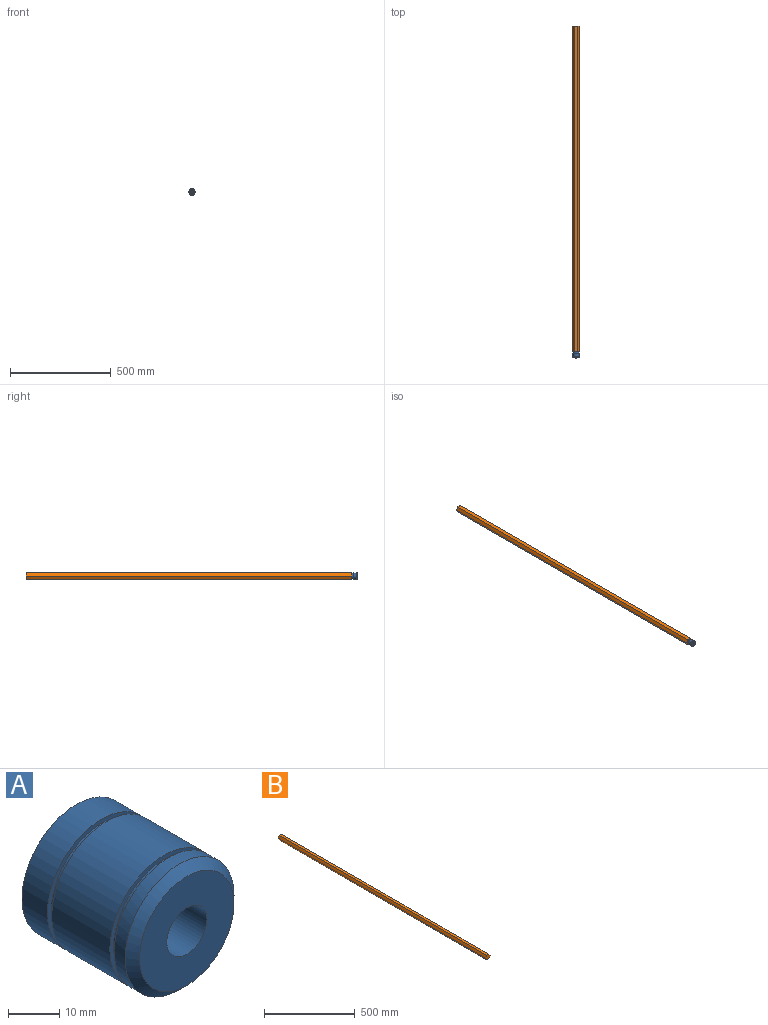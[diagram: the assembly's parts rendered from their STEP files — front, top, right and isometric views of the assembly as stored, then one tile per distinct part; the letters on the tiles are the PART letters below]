
ASSEMBLY  parts=2 mates=1
PART A: 14 faces, bbox 30x30.4x30 mm
  f0: plane 26x26mm, normal (0,-1,0), area 435.9mm2, adj f11,f12
  f1: plane 30x30mm, normal (0,1,0), area 706.9mm2, adj f2
  f2: cylinder r=15mm len=30mm, axis (0,-1,0), area 659.7mm2, adj f1,f3
  f3: plane 30x30mm, normal (0,-1,0), area 91.1mm2, adj f2,f4
  f4: cylinder r=14mm len=28mm, axis (0,-1,0), area 105.6mm2, adj f3,f5
  f5: plane 30x30mm, normal (0,1,0), area 91.1mm2, adj f4,f6
  f6: cylinder r=15mm len=30mm, axis (0,-1,0), area 1508mm2, adj f5,f7
  f7: plane 30x30mm, normal (0,-1,0), area 91.1mm2, adj f6,f8
  f8: cylinder r=14mm len=28mm, axis (0,-1,0), area 105.6mm2, adj f7,f9
  f9: plane 30x30mm, normal (0,1,0), area 91.1mm2, adj f8,f10
  f10: cylinder r=15mm len=30mm, axis (0,-1,0), area 282.7mm2, adj f9,f11
  f11: cone r=13mm half-angle=45deg, axis (0,1,0), area 248.8mm2, adj f0,f10
  f12: cylinder r=5.5mm len=20mm, axis (0,-1,0), area 691.2mm2, adj f0,f13
  f13: cone r=0mm half-angle=59deg, axis (0,-1,0), area 110.9mm2, adj f12
PART B: 14 faces, bbox 34.6x1620x30 mm
  f0: plane 1618x15mm, normal (0.87,0,-0.5), area 28024.6mm2, adj f1,f5,f6,f13
  f1: plane 1618x15mm, normal (0.87,0,0.5), area 28024.6mm2, adj f0,f2,f6,f11
  f2: plane 1618x17.32mm, normal (0,0,1), area 28024.6mm2, adj f1,f3,f6,f9
  f3: plane 1618x15mm, normal (-0.87,0,0.5), area 28024.6mm2, adj f2,f4,f6,f8
  f4: plane 1618x15mm, normal (-0.87,0,-0.5), area 28024.6mm2, adj f3,f5,f6,f10
  f5: plane 1618x17.32mm, normal (0,0,-1), area 28024.6mm2, adj f0,f4,f6,f12
  f6: plane 34.64x30mm, normal (0,-1,0), area 779.4mm2, adj f0,f1,f2,f3,f4,f5
  f7: plane 30.02x26mm, normal (0,1,0), area 585.4mm2, adj f8,f9,f10,f11,f12,f13
  f8: plane 15x9.82mm, normal (-0.61,0.71,0.35), area 45.7mm2, adj f3,f7,f9,f10
  f9: plane 17.32x2mm, normal (0,0.71,0.71), area 45.7mm2, adj f2,f7,f8,f11
  f10: plane 15x9.82mm, normal (-0.61,0.71,-0.35), area 45.7mm2, adj f4,f7,f8,f12
  f11: plane 15x9.82mm, normal (0.61,0.71,0.35), area 45.7mm2, adj f1,f7,f9,f13
  f12: plane 17.32x2mm, normal (0,0.71,-0.71), area 45.7mm2, adj f5,f7,f10,f13
  f13: plane 15x9.82mm, normal (0.61,0.71,-0.35), area 45.7mm2, adj f0,f7,f11,f12
PLACE A t=(0,-998.55,-80)mm
PLACE B at identity
MATE fastened A.f2 <-> B.f6  axis (0,1,0) through (0,-1620,0)mm
